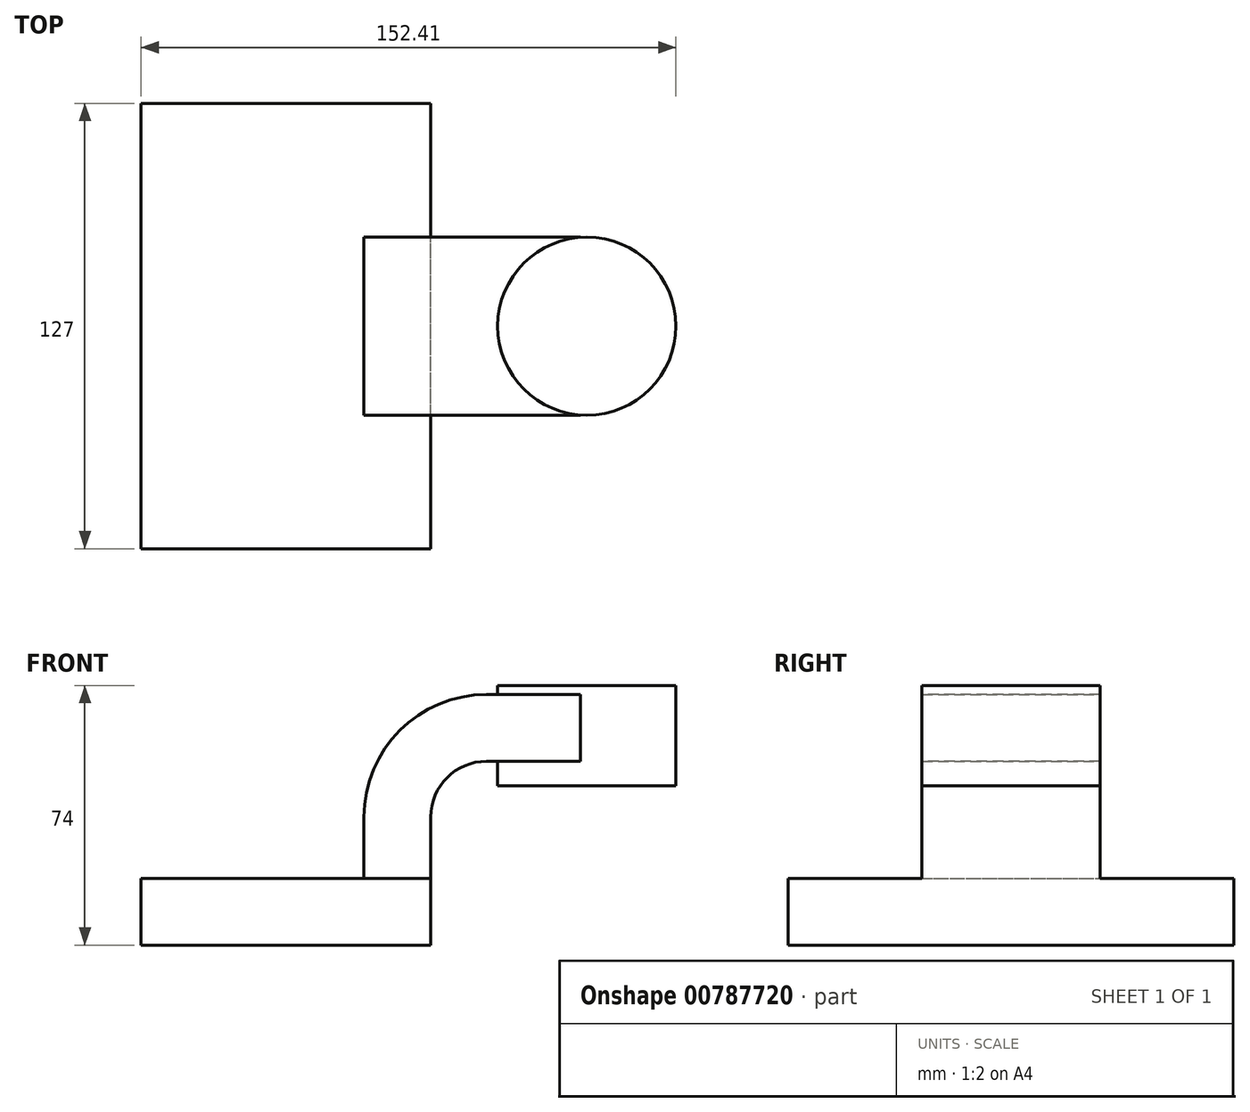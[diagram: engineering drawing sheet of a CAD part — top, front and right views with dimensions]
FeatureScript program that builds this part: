
annotation { "Feature Type Name" : "Feature", "Feature Type Description" : "" }
export const myFeature = defineFeature(function(context is Context, id is Id, definition is map)
    precondition{}
    {
        {
            var Q0;
            Q0=qCreatedBy(makeId("Front.planeOp"),FACE);
            var sketch = newSketch(context, id + "F0", { "sketchPlane" : qUnion([Q0])});
            skLineSegment(sketch, "E0.bottom", {"start": v(41.27, 9.53) * mm, "end": v(-41.28, 9.53) * mm});
            skLineSegment(sketch, "E0.top", {"start": v(41.28, -9.52) * mm, "end": v(-41.27, -9.52) * mm});
            skLineSegment(sketch, "E0.left", {"start": v(41.28, 9.53) * mm, "end": v(41.28, -9.52) * mm});
            skLineSegment(sketch, "E0.right", {"start": v(-41.28, 9.53) * mm, "end": v(-41.27, -9.52) * mm});
            skPoint(sketch, "E0.middle", {"position": v(0, 0) * mm});
            skLineSegment(sketch, "E1.bottom", {"start": v(111.13, 64.47) * mm, "end": v(60.33, 64.47) * mm});
            skLineSegment(sketch, "E1.top", {"start": v(111.13, 35.9) * mm, "end": v(60.33, 35.9) * mm});
            skLineSegment(sketch, "E1.left", {"start": v(111.13, 64.47) * mm, "end": v(111.13, 35.9) * mm});
            skLineSegment(sketch, "E1.right", {"start": v(60.33, 64.47) * mm, "end": v(60.33, 35.9) * mm});
            skPoint(sketch, "E1.middle", {"position": v(85.73, 50.19) * mm});
            skLineSegment(sketch, "E2", {"start": v(41.27, 9.53) * mm, "end": v(41.27, 27) * mm});
            skArc(sketch, "E3", {"start": v(41.28, 27) * mm, "mid": v(45.92, 38.23) * mm, "end": v(57.15, 42.88) * mm});
            skLineSegment(sketch, "E4", {"start": v(57.15, 42.88) * mm, "end": v(83.9, 42.88) * mm});
            skLineSegment(sketch, "E5.0", {"start": v(57.15, 61.93) * mm, "end": v(83.9, 61.93) * mm});
            skArc(sketch, "E5.1", {"start": v(22.23, 27) * mm, "mid": v(32.45, 51.7) * mm, "end": v(57.15, 61.93) * mm});
            skLineSegment(sketch, "E5.2", {"start": v(22.23, 9.53) * mm, "end": v(22.23, 27) * mm});
            skFitSpline(sketch, "E6", {"points": [v(-41.28, 9.53) * mm, v(57.15, 61.93) * mm], "startDerivative": vector(124.14, 7.25) * mm, "endDerivative": vector(126.86, -7.38) * mm});
            skLineSegment(sketch, "E7", {"start": v(83.9, 61.93) * mm, "end": v(83.9, 42.88) * mm});
            skLineSegment(sketch, "E8", {"start": v(85.73, 64.47) * mm, "end": v(85.73, 35.9) * mm});
            skSolve(sketch);
        }
        {
            var Q0;
            Q0=makeQuery(id+"F0.imprint","IMPRINT",FACE,{"disambiguationData":[TD([[makeQuery(id+"F0.imprint","IMPRINT",EDGE,{"derivedFrom":sQuery(id+"F0.wireOp",EDGE,"E0.top")}),-1.0]])]});
            extrude(context, id + "F1", {"entities" : qUnion([Q0]), "endBound" : BoundingType.SYMMETRIC, "depth" : 127 * mm, "offsetDistance" : 25.4 * mm});
        }
        {
            var Q0;
            Q0=makeQuery(id+"F0.imprint","IMPRINT",FACE,{"disambiguationData":[TD([[makeQuery(id+"F0.imprint","IMPRINT",EDGE,{"derivedFrom":sQuery(id+"F0.wireOp",EDGE,"E5.1")}),1.0]])]});
            extrude(context, id + "F2", {"entities" : qUnion([Q0]), "operationType" : NewBodyOperationType.ADD, "endBound" : BoundingType.SYMMETRIC, "depth" : 25.4 * mm, "offsetDistance" : 25.4 * mm});
        }
        {
            var Q0;
            {var subQ1=sQuery(id+"F0.wireOp",EDGE,"E2");Q0=makeQuery(id+"F0.imprint","IMPRINT",FACE,{"disambiguationData":[TD([[makeQuery(id+"F0.imprint","IMPRINT",EDGE,{"derivedFrom":subQ1}),1.0]])]});}
            var Q1;
            {var subQ5=sQuery(id+"F0.wireOp",EDGE,"E7");Q1=makeQuery(id+"F0.imprint","IMPRINT",FACE,{"disambiguationData":[TD([[makeQuery(id+"F0.imprint","IMPRINT",EDGE,{"derivedFrom":subQ5}),-1.0]])]});}
            extrude(context, id + "F3", {"entities" : qUnion([Q0, Q1]), "operationType" : NewBodyOperationType.ADD, "endBound" : BoundingType.SYMMETRIC, "depth" : 50.8 * mm, "offsetDistance" : 25.4 * mm});
        }
        {
            var Q0;
            {var subQ0=sQuery(id+"F0.wireOp",EDGE,"E1.left");Q0=makeQuery(id+"F0.imprint","IMPRINT",FACE,{"disambiguationData":[TD([[makeQuery(id+"F0.imprint","IMPRINT",EDGE,{"derivedFrom":subQ0}),-1.0]])]});}
            var Q1;
            Q1=sQuery(id+"F0.wireOp",EDGE,"E8");
            revolve(context, id + "F4", {"operationType" : NewBodyOperationType.ADD, "surfaceOperationType" : NewSurfaceOperationType.NEW, "entities" : qUnion([Q0]), "axis" : qUnion([Q1]), "revolveType" : RevolveType.FULL});
        }
    });
